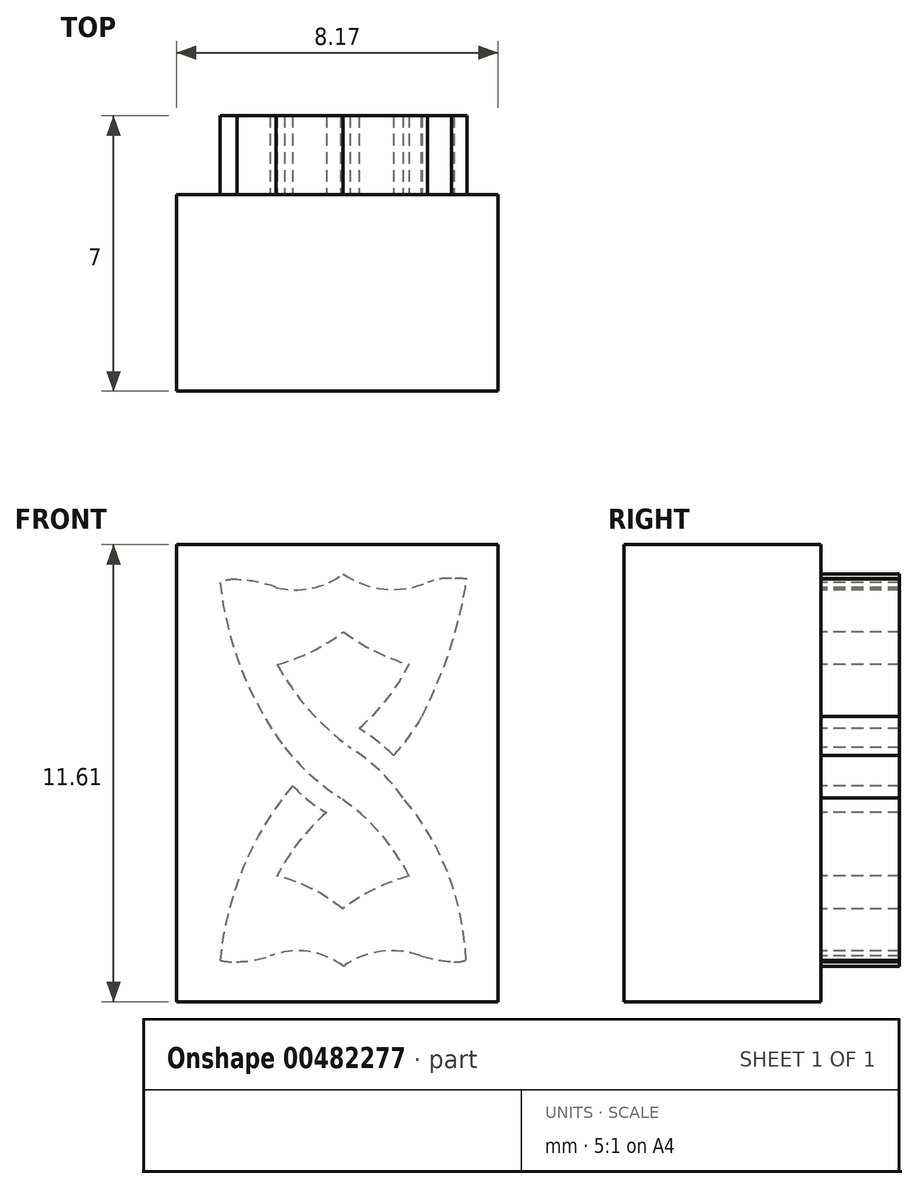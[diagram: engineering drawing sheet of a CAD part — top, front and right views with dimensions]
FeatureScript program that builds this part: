
annotation { "Feature Type Name" : "Feature", "Feature Type Description" : "" }
export const myFeature = defineFeature(function(context is Context, id is Id, definition is map)
    precondition{}
    {
        {
            var Q0;
            Q0=qCreatedBy(makeId("Front.planeOp"),FACE);
            var sketch = newSketch(context, id + "F0", { "sketchPlane" : qUnion([Q0])});
            skPoint(sketch, "E0.middle", {"position": v(0, 0) * mm});
            skPoint(sketch, "E0.left.start.orphan", {"position": v(-5, 5) * mm});
            skPoint(sketch, "E0.right.start.orphan", {"position": v(5, 5) * mm});
            skArc(sketch, "E1", {"start": v(-0.07, 5) * mm, "mid": v(0.98, 4.62) * mm, "end": v(2.07, 4.8) * mm});
            skArc(sketch, "E2", {"start": v(2.68, 4.9) * mm, "mid": v(2.37, 4.88) * mm, "end": v(2.07, 4.8) * mm});
            skArc(sketch, "E3", {"start": v(3.07, 4.88) * mm, "mid": v(2.88, 4.9) * mm, "end": v(2.68, 4.9) * mm});
            skPoint(sketch, "E3.startSnap0", {"position": v(2.37, 4.88) * mm});
            skArc(sketch, "E4", {"start": v(1.93, 1.39) * mm, "mid": v(2.64, 3.08) * mm, "end": v(3.07, 4.88) * mm});
            skArc(sketch, "E5", {"start": v(1.2, 0.4) * mm, "mid": v(1.6, 0.87) * mm, "end": v(1.93, 1.39) * mm});
            skArc(sketch, "E6", {"start": v(1.2, 0.4) * mm, "mid": v(0.8, 0.77) * mm, "end": v(0.33, 1.09) * mm});
            skArc(sketch, "E7", {"start": v(0.33, 1.09) * mm, "mid": v(1.05, 1.83) * mm, "end": v(1.6, 2.7) * mm});
            skArc(sketch, "E8", {"start": v(-0.06, 3.54) * mm, "mid": v(0.74, 3.05) * mm, "end": v(1.6, 2.7) * mm});
            skArc(sketch, "E9", {"start": v(-1.75, 2.7) * mm, "mid": v(-0.86, 3.04) * mm, "end": v(-0.06, 3.54) * mm});
            skArc(sketch, "E10", {"start": v(-1.75, 2.7) * mm, "mid": v(-0.93, 1.55) * mm, "end": v(0.1, 0.6) * mm});
            skArc(sketch, "E11", {"start": v(1.46, -0.68) * mm, "mid": v(0.84, 0.03) * mm, "end": v(0.1, 0.6) * mm});
            skArc(sketch, "E12", {"start": v(3.05, -4.8) * mm, "mid": v(2.6, -2.61) * mm, "end": v(1.46, -0.68) * mm});
            skArc(sketch, "E13", {"start": v(2.75, -4.85) * mm, "mid": v(2.9, -4.84) * mm, "end": v(3.05, -4.8) * mm});
            skArc(sketch, "E14", {"start": v(1.91, -4.7) * mm, "mid": v(2.32, -4.8) * mm, "end": v(2.75, -4.85) * mm});
            skArc(sketch, "E15", {"start": v(1.91, -4.7) * mm, "mid": v(0.9, -4.59) * mm, "end": v(-0.06, -4.96) * mm});
            skArc(sketch, "E16", {"start": v(-0.06, -4.96) * mm, "mid": v(-0.96, -4.59) * mm, "end": v(-1.93, -4.7) * mm});
            skArc(sketch, "E17", {"start": v(-2.78, -4.85) * mm, "mid": v(-2.35, -4.8) * mm, "end": v(-1.93, -4.7) * mm});
            skArc(sketch, "E18", {"start": v(-3.2, -4.8) * mm, "mid": v(-2.99, -4.84) * mm, "end": v(-2.78, -4.85) * mm});
            skArc(sketch, "E19", {"start": v(-1.35, -0.37) * mm, "mid": v(-2.6, -2.45) * mm, "end": v(-3.2, -4.8) * mm});
            skArc(sketch, "E20", {"start": v(-1.35, -0.37) * mm, "mid": v(-0.95, -0.75) * mm, "end": v(-0.49, -1.06) * mm});
            skArc(sketch, "E21", {"start": v(-0.49, -1.06) * mm, "mid": v(-1.2, -1.8) * mm, "end": v(-1.75, -2.67) * mm});
            skArc(sketch, "E22", {"start": v(-0.08, -3.5) * mm, "mid": v(-0.87, -3) * mm, "end": v(-1.75, -2.67) * mm});
            skArc(sketch, "E23", {"start": v(1.6, -2.67) * mm, "mid": v(0.72, -3) * mm, "end": v(-0.08, -3.5) * mm});
            skArc(sketch, "E24", {"start": v(1.6, -2.67) * mm, "mid": v(0.86, -1.57) * mm, "end": v(-0.14, -0.68) * mm});
            skArc(sketch, "E25", {"start": v(-1.56, 0.6) * mm, "mid": v(-0.9, -0.1) * mm, "end": v(-0.14, -0.68) * mm});
            skArc(sketch, "E26", {"start": v(-3.2, 4.79) * mm, "mid": v(-2.65, 2.59) * mm, "end": v(-1.56, 0.6) * mm});
            skArc(sketch, "E27", {"start": v(-2.76, 4.86) * mm, "mid": v(-2.98, 4.85) * mm, "end": v(-3.2, 4.79) * mm});
            skArc(sketch, "E28", {"start": v(-1.77, 4.67) * mm, "mid": v(-2.26, 4.8) * mm, "end": v(-2.76, 4.86) * mm});
            skArc(sketch, "E29", {"start": v(-1.77, 4.67) * mm, "mid": v(-0.88, 4.64) * mm, "end": v(-0.07, 5) * mm});
            skPoint(sketch, "E0.top.end.orphan", {"position": v(5, -5) * mm});
            skPoint(sketch, "E0.top.start.orphan", {"position": v(-5, -5) * mm});
            skLineSegment(sketch, "E30.bottom", {"start": v(-4.3, 5.75) * mm, "end": v(3.87, 5.75) * mm});
            skLineSegment(sketch, "E30.top", {"start": v(-4.3, -5.86) * mm, "end": v(3.87, -5.86) * mm});
            skLineSegment(sketch, "E30.left", {"start": v(-4.3, 5.75) * mm, "end": v(-4.3, -5.86) * mm});
            skLineSegment(sketch, "E30.right", {"start": v(3.87, 5.75) * mm, "end": v(3.87, -5.86) * mm});
            skSolve(sketch);
        }
        {
            var Q0;
            Q0=makeQuery(id+"F0.imprint","IMPRINT",FACE,{"disambiguationData":[TD([[makeQuery(id+"F0.imprint","IMPRINT",EDGE,{"derivedFrom":sQuery(id+"F0.wireOp",EDGE,"E1")}),-1.0]])]});
            extrude(context, id + "F1", {"entities" : qUnion([Q0]), "oppositeDirection" : true, "depth" : 2 * mm});
        }
        {
            var Q0;
            Q0=makeQuery(id+"F0.imprint","IMPRINT",FACE,{"disambiguationData":[TD([[makeQuery(id+"F0.imprint","IMPRINT",EDGE,{"derivedFrom":sQuery(id+"F0.wireOp",EDGE,"E1")}),1.0]])]});
            var Q1;
            Q1=makeQuery(id+"F1.opExtrude","CAP_FACE",FACE,{"disambiguationData":[OSD([sQuery(id+"F0.wireOp",EDGE,"E1"),sQuery(id+"F0.wireOp",EDGE,"E2"),sQuery(id+"F0.wireOp",EDGE,"E3"),sQuery(id+"F0.wireOp",EDGE,"E4"),sQuery(id+"F0.wireOp",EDGE,"E5"),sQuery(id+"F0.wireOp",EDGE,"E6"),sQuery(id+"F0.wireOp",EDGE,"E7"),sQuery(id+"F0.wireOp",EDGE,"E8"),sQuery(id+"F0.wireOp",EDGE,"E9"),sQuery(id+"F0.wireOp",EDGE,"E10"),sQuery(id+"F0.wireOp",EDGE,"E11"),sQuery(id+"F0.wireOp",EDGE,"E12"),sQuery(id+"F0.wireOp",EDGE,"E13"),sQuery(id+"F0.wireOp",EDGE,"E14"),sQuery(id+"F0.wireOp",EDGE,"E15"),sQuery(id+"F0.wireOp",EDGE,"E16"),sQuery(id+"F0.wireOp",EDGE,"E17"),sQuery(id+"F0.wireOp",EDGE,"E18"),sQuery(id+"F0.wireOp",EDGE,"E19"),sQuery(id+"F0.wireOp",EDGE,"E20"),sQuery(id+"F0.wireOp",EDGE,"E21"),sQuery(id+"F0.wireOp",EDGE,"E22"),sQuery(id+"F0.wireOp",EDGE,"E23"),sQuery(id+"F0.wireOp",EDGE,"E24"),sQuery(id+"F0.wireOp",EDGE,"E25"),sQuery(id+"F0.wireOp",EDGE,"E26"),sQuery(id+"F0.wireOp",EDGE,"E27"),sQuery(id+"F0.wireOp",EDGE,"E28"),sQuery(id+"F0.wireOp",EDGE,"E29")])],"isStart":false});
            var Q2;
            Q2=makeQuery(id+"F0.imprint","IMPRINT",FACE,{"disambiguationData":[TD([[makeQuery(id+"F0.imprint","IMPRINT",EDGE,{"derivedFrom":sQuery(id+"F0.wireOp",EDGE,"E1")}),-1.0]])]});
            extrude(context, id + "F2", {"entities" : qUnion([Q0, Q1, Q2]), "operationType" : NewBodyOperationType.ADD, "depth" : 5 * mm});
        }
    });
